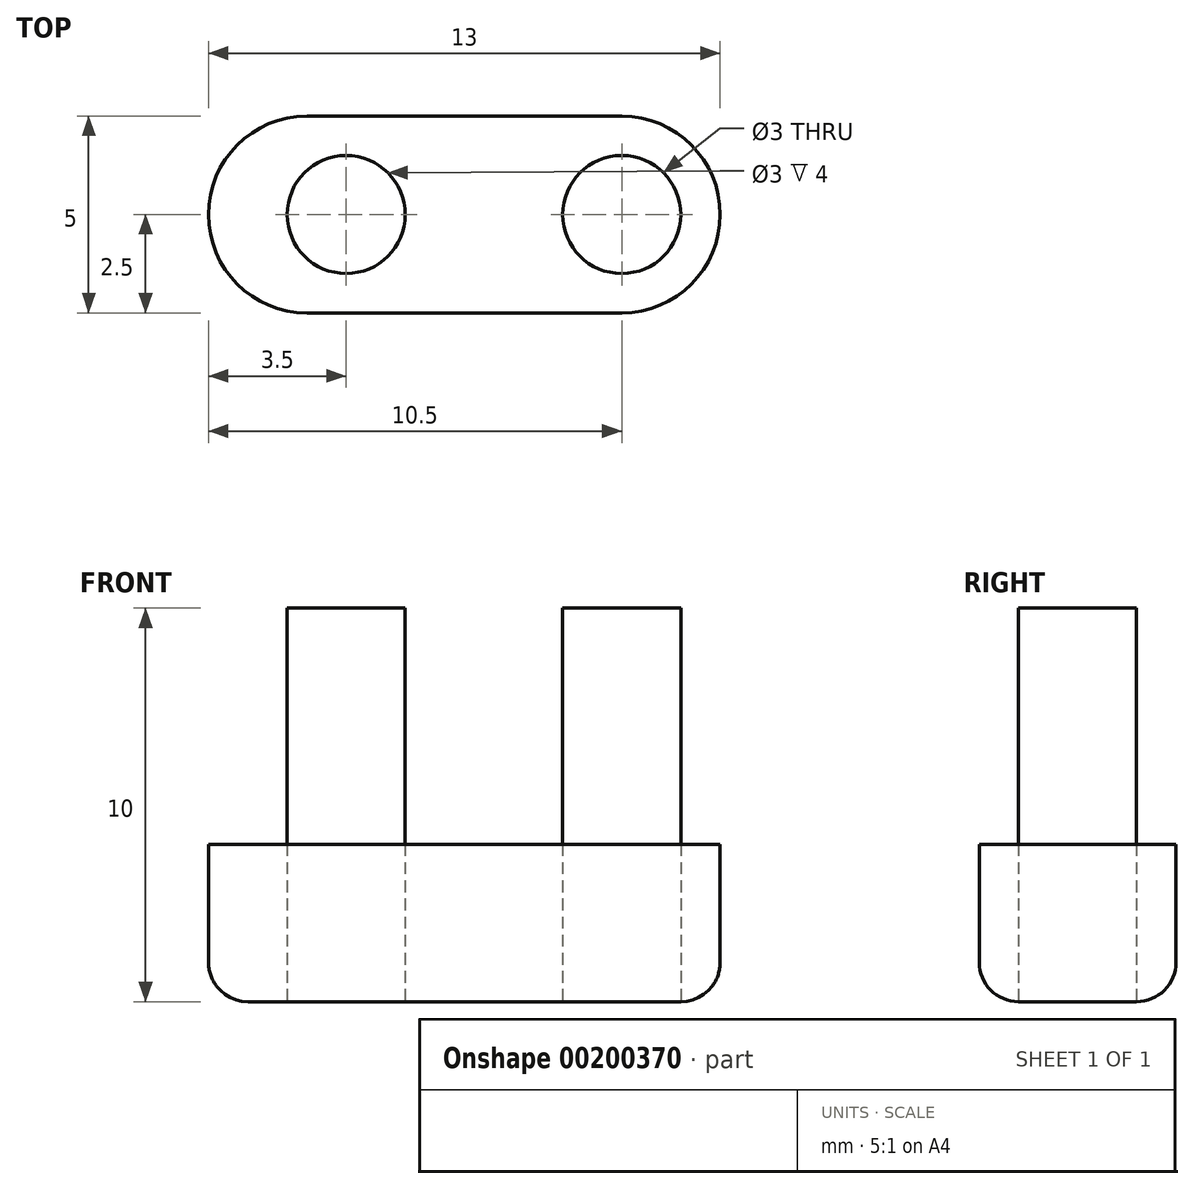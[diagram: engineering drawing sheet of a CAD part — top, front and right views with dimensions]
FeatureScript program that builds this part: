
annotation { "Feature Type Name" : "Feature", "Feature Type Description" : "" }
export const myFeature = defineFeature(function(context is Context, id is Id, definition is map)
    precondition{}
    {
        {
            var Q0;
            Q0=qCreatedBy(makeId("Top.planeOp"),FACE);
            var sketch = newSketch(context, id + "F0", { "sketchPlane" : qUnion([Q0])});
            skLineSegment(sketch, "E0.bottom", {"start": v(-4, 2.5) * mm, "end": v(4, 2.5) * mm});
            skLineSegment(sketch, "E0.top", {"start": v(-4, -2.5) * mm, "end": v(4, -2.5) * mm});
            skLineSegment(sketch, "E0.left", {"start": v(-6.5, 0) * mm, "end": v(-6.5, 0) * mm});
            skLineSegment(sketch, "E0.right", {"start": v(6.5, 0) * mm, "end": v(6.5, 0) * mm});
            skPoint(sketch, "E0.middle", {"position": v(0, 0) * mm});
            skPoint(sketch, "E1", {"position": v(-3, 0) * mm});
            skPoint(sketch, "E2", {"position": v(4, 0) * mm});
            skPoint(sketch, "E3.visualSharp", {"position": v(6.5, 2.5) * mm});
            skArc(sketch, "E3.filletArc", {"start": v(6.5, 0) * mm, "mid": v(5.77, 1.77) * mm, "end": v(4, 2.5) * mm});
            skPoint(sketch, "E4.visualSharp", {"position": v(6.5, -2.5) * mm});
            skArc(sketch, "E4.filletArc", {"start": v(4, -2.5) * mm, "mid": v(5.77, -1.77) * mm, "end": v(6.5, 0) * mm});
            skPoint(sketch, "E5.visualSharp", {"position": v(-6.5, -2.5) * mm});
            skArc(sketch, "E5.filletArc", {"start": v(-6.5, 0) * mm, "mid": v(-5.77, -1.77) * mm, "end": v(-4, -2.5) * mm});
            skPoint(sketch, "E6.visualSharp", {"position": v(-6.5, 2.5) * mm});
            skArc(sketch, "E6.filletArc", {"start": v(-4, 2.5) * mm, "mid": v(-5.77, 1.77) * mm, "end": v(-6.5, 0) * mm});
            skCircle(sketch, "E7", {"center": v(4, 0) * mm, "radius": 1.5 * mm});
            skCircle(sketch, "E8", {"center": v(-3, 0) * mm, "radius": 1.5 * mm});
            skSolve(sketch);
        }
        {
            var Q0;
            Q0=makeQuery(id+"F0.imprint","IMPRINT",FACE,{"disambiguationData":[TD([[makeQuery(id+"F0.imprint","IMPRINT",EDGE,{"derivedFrom":sQuery(id+"F0.wireOp",EDGE,"E7")}),1.0]])]});
            var Q1;
            Q1=makeQuery(id+"F0.imprint","IMPRINT",FACE,{"disambiguationData":[TD([[makeQuery(id+"F0.imprint","IMPRINT",EDGE,{"derivedFrom":sQuery(id+"F0.wireOp",EDGE,"E8")}),1.0]])]});
            extrude(context, id + "F1", {"entities" : qUnion([Q0, Q1]), "depth" : 10 * mm});
        }
        {
            var Q0;
            Q0=makeQuery(id+"F0.imprint","IMPRINT",FACE,{"disambiguationData":[TD([[makeQuery(id+"F0.imprint","IMPRINT",EDGE,{"derivedFrom":sQuery(id+"F0.wireOp",EDGE,"E0.bottom")}),-1.0]])]});
            extrude(context, id + "F2", {"entities" : qUnion([Q0]), "depth" : 4 * mm});
        }
        {
            var Q0;
            Q0=makeQuery(id+"F2.opExtrude","CAP_EDGE",EDGE,{"disambiguationData":[OSD([sQuery(id+"F0.wireOp",EDGE,"E0.bottom")])],"isStart":true});
            var Q1;
            Q1=makeQuery(id+"F2.opExtrude","CAP_EDGE",EDGE,{"disambiguationData":[OSD([sQuery(id+"F0.wireOp",EDGE,"E5.filletArc"),sQuery(id+"F0.wireOp",EDGE,"E6.filletArc")])],"isStart":true});
            fillet(context, id + "F3", {"entities" : qUnion([Q0, Q1]), "radius" : 1 * mm, "tangentPropagation" : true, "allowEdgeOverflow" : false});
        }
    });
